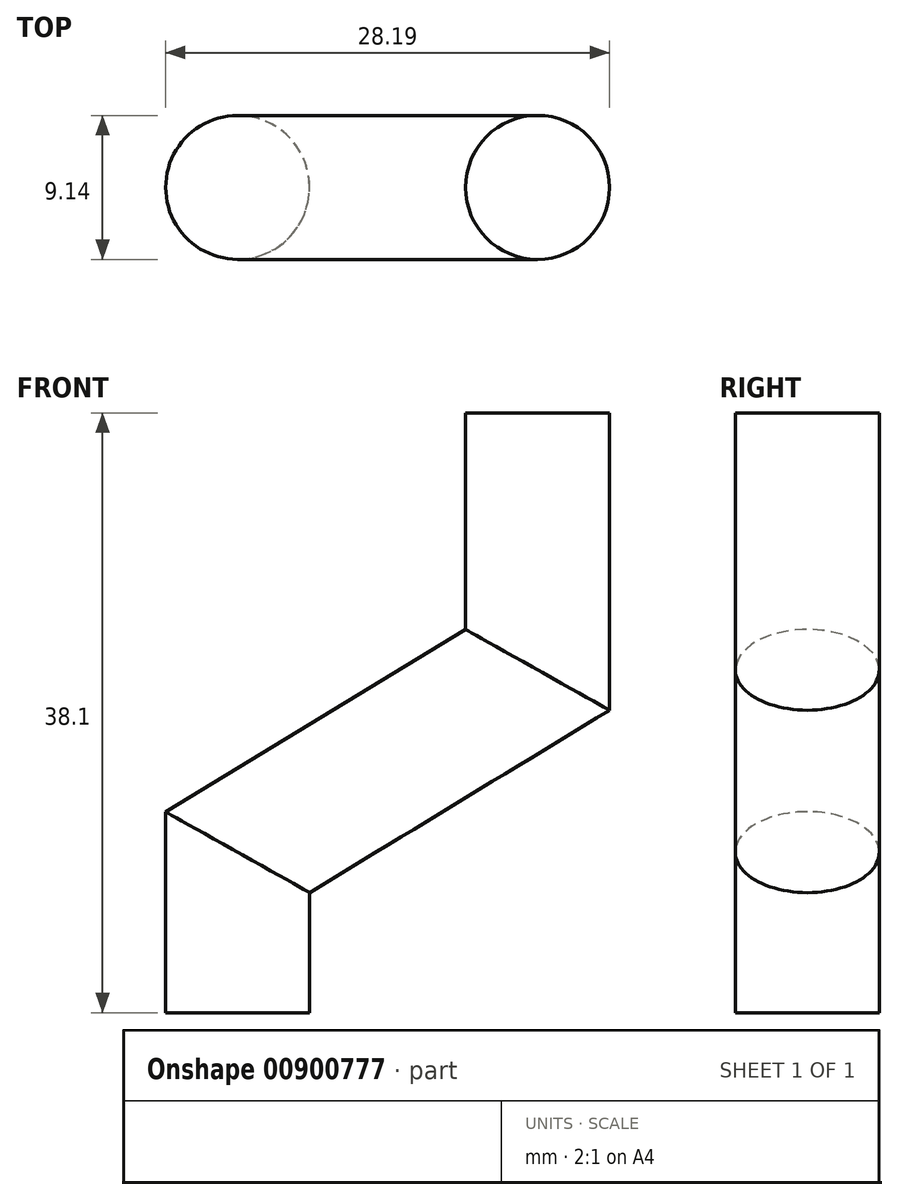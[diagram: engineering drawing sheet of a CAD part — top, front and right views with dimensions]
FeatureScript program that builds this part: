
annotation { "Feature Type Name" : "Feature", "Feature Type Description" : "" }
export const myFeature = defineFeature(function(context is Context, id is Id, definition is map)
    precondition{}
    {
        {
            var Q0;
            Q0=qCreatedBy(makeId("Front.planeOp"),FACE);
            var sketch = newSketch(context, id + "F0", { "sketchPlane" : qUnion([Q0])});
            skLineSegment(sketch, "E0", {"start": v(-19.05, 0) * mm, "end": v(-19.05, 13.81) * mm});
            skLineSegment(sketch, "E1", {"start": v(-19.05, 13.81) * mm, "end": v(0, 25.4) * mm});
            skLineSegment(sketch, "E2", {"start": v(0, 25.4) * mm, "end": v(0, 38.1) * mm});
            skSolve(sketch);
        }
        {
            var Q0;
            Q0=qCreatedBy(makeId("Top.planeOp"),FACE);
            var sketch = newSketch(context, id + "F1", { "sketchPlane" : qUnion([Q0])});
            skCircle(sketch, "E3", {"center": v(-12.61, 0) * mm, "radius": 4.57 * mm});
            skSolve(sketch);
        }
        {
            var Q0;
            Q0=makeQuery(id+"F1.imprint","IMPRINT",FACE,{"disambiguationData":[TD([[makeQuery(id+"F1.imprint","IMPRINT",EDGE,{"derivedFrom":sQuery(id+"F1.wireOp",EDGE,"E3")}),1.0]])]});
            var Q1;
            Q1=sQuery(id+"F0.wireOp",EDGE,"E0");
            var Q2;
            Q2=sQuery(id+"F0.wireOp",EDGE,"E1");
            var Q3;
            Q3=sQuery(id+"F0.wireOp",EDGE,"E2");
            sweep(context, id + "F2", {"profiles" : qUnion([Q0]), "path" : qUnion([Q1, Q2, Q3])});
        }
    });
